# Revit family: Alcorque Rel
name_source: partatom
category: Furniture
units: mm (PartAtom-declared; Revit-internal decimal feet)

## family parameters
Always vertical = Yes
Cut with Voids When Loaded = No
OmniClass Number = 23.40.20.00
OmniClass Title = General Furniture and Specialties
Room Calculation Point = No
Shared = No
Work Plane-Based = No

## types (8) — shared parameters
Description = Alcorque fabricado en malla electrosoldada de 34 x 38 mm, entre ejes, pletina portante de 30 x 2mm, separador cuadrado de 4 mm
entregirado.
Ficha_Tecnica = https://www.benito.com
Material = Acero galvanizado
URL_Producto = https://www.benito.com
zero-valued in all types: D, Default Elevation, H

## per-type parameters (varying)
| type | A | B | Referencia |
| Alcorque Rel-A80-490mm | 0 m | 0 m | A80 |
| Alcorque Rel-A81-560mm | 1 m | 1 m | A81 |
| Alcorque Rel-A82-695mm | 1 m | 1 m | A82 |
| Alcorque Rel-A83-765mm | 1 m | 1 m | A83 |
| Alcorque Rel-A84-900mm | 1 m | 1 m | A84 |
| Alcorque Rel-A85-970mm | 1 m | 1 m | A85 |
| Alcorque Rel-A86-1105mm | 1 m | 1 m | A86 |
| Alcorque Rel-A87-1175mm | 1 m | 1 m | A87 |

type visibility flags: 8 boolean params named "<type name>" — each type sets only its own to Yes (folded from table)

## geometry (parser evidence)
native form markers: Blend x4, Sweep x18
no freeform markers — native parametric forms only
